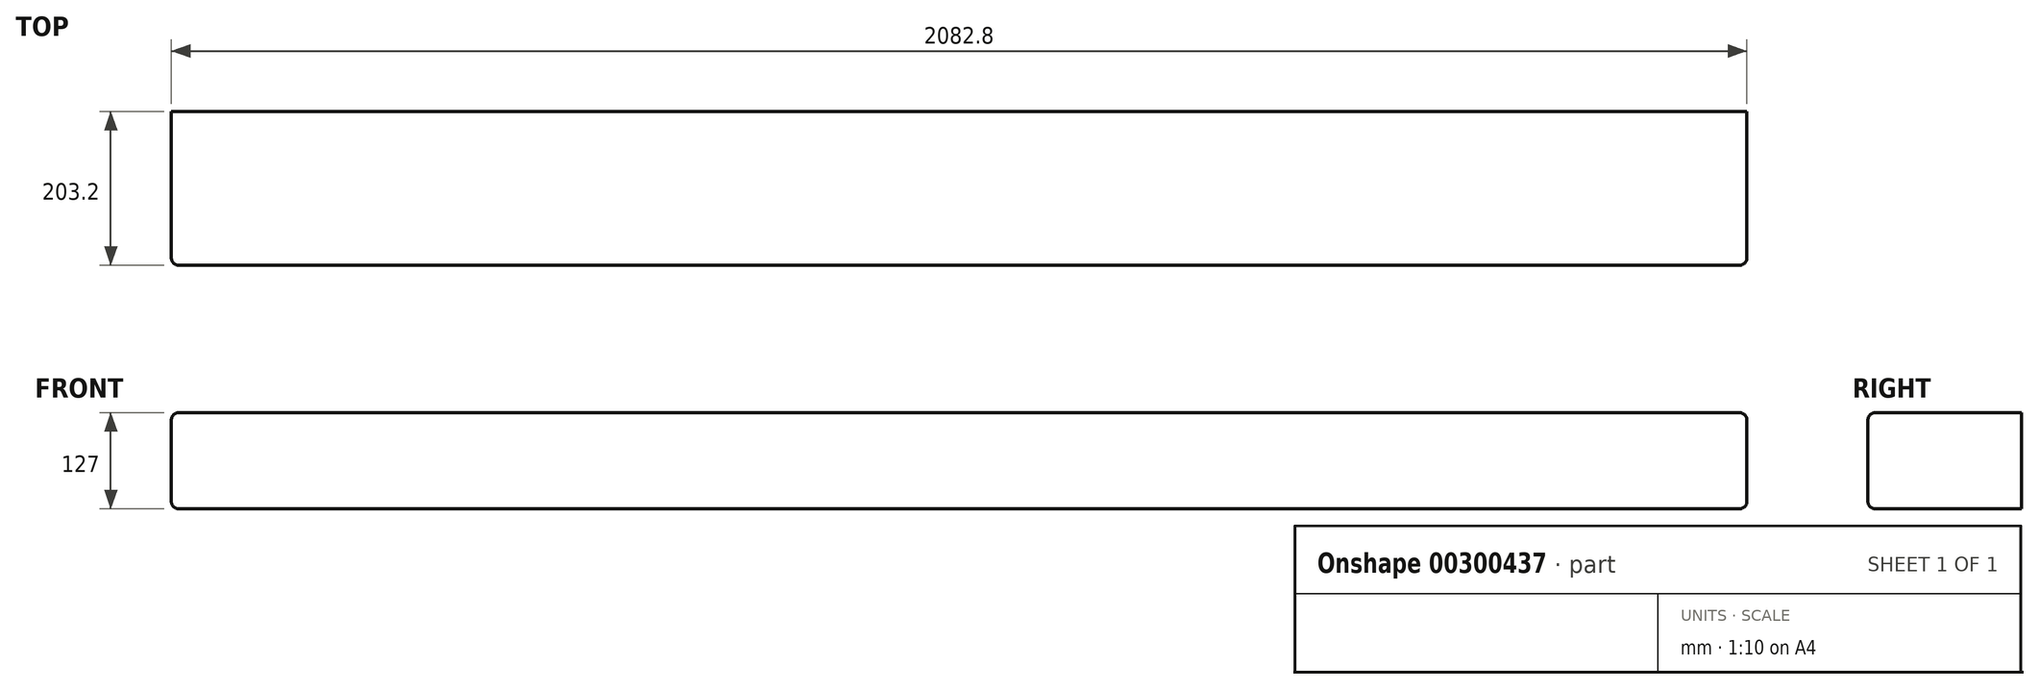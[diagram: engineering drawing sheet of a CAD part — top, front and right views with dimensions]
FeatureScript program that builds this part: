
annotation { "Feature Type Name" : "Feature", "Feature Type Description" : "" }
export const myFeature = defineFeature(function(context is Context, id is Id, definition is map)
    precondition{}
    {
        {
            var Q0;
            Q0=qCreatedBy(makeId("Right.planeOp"),FACE);
            var sketch = newSketch(context, id + "F0", { "sketchPlane" : qUnion([Q0])});
            skLineSegment(sketch, "E0.bottom", {"start": v(-101.6, 63.5) * mm, "end": v(101.6, 63.5) * mm});
            skLineSegment(sketch, "E0.top", {"start": v(-101.6, -63.5) * mm, "end": v(101.6, -63.5) * mm});
            skLineSegment(sketch, "E0.left", {"start": v(-101.6, 63.5) * mm, "end": v(-101.6, -63.5) * mm});
            skLineSegment(sketch, "E0.right", {"start": v(101.6, 63.5) * mm, "end": v(101.6, -63.5) * mm});
            skSolve(sketch);
        }
        {
            var Q0;
            Q0=makeQuery(id+"F0.imprint","IMPRINT",FACE,{"disambiguationData":[TD([[makeQuery(id+"F0.imprint","IMPRINT",EDGE,{"derivedFrom":sQuery(id+"F0.wireOp",EDGE,"E0.bottom")}),-1.0]])]});
            extrude(context, id + "F1", {"entities" : qUnion([Q0]), "endBound" : BoundingType.SYMMETRIC, "depth" : 2082.8 * mm});
        }
        {
            var Q0;
            Q0=makeQuery(id+"F1.opExtrude","SWEPT_EDGE",EDGE,{"disambiguationData":[OSD([sQuery(id+"F0.wireOp",EDGE,"E0.bottom"),sQuery(id+"F0.wireOp",EDGE,"E0.left")])]});
            var Q1;
            Q1=makeQuery(id+"F1.opExtrude","CAP_EDGE",EDGE,{"disambiguationData":[OSD([sQuery(id+"F0.wireOp",EDGE,"E0.bottom")])],"isStart":true});
            var Q2;
            Q2=makeQuery(id+"F1.opExtrude","CAP_EDGE",EDGE,{"disambiguationData":[OSD([sQuery(id+"F0.wireOp",EDGE,"E0.left")])],"isStart":true});
            var Q3;
            Q3=makeQuery(id+"F1.opExtrude","CAP_EDGE",EDGE,{"disambiguationData":[OSD([sQuery(id+"F0.wireOp",EDGE,"E0.top")])],"isStart":true});
            var Q4;
            Q4=makeQuery(id+"F1.opExtrude","SWEPT_EDGE",EDGE,{"disambiguationData":[OSD([sQuery(id+"F0.wireOp",EDGE,"E0.top"),sQuery(id+"F0.wireOp",EDGE,"E0.left")])]});
            var Q5;
            Q5=makeQuery(id+"F1.opExtrude","CAP_EDGE",EDGE,{"disambiguationData":[OSD([sQuery(id+"F0.wireOp",EDGE,"E0.bottom")])],"isStart":false});
            var Q6;
            Q6=makeQuery(id+"F1.opExtrude","CAP_EDGE",EDGE,{"disambiguationData":[OSD([sQuery(id+"F0.wireOp",EDGE,"E0.left")])],"isStart":false});
            var Q7;
            Q7=makeQuery(id+"F1.opExtrude","CAP_EDGE",EDGE,{"disambiguationData":[OSD([sQuery(id+"F0.wireOp",EDGE,"E0.top")])],"isStart":false});
            fillet(context, id + "F2", {"entities" : qUnion([Q0, Q1, Q2, Q3, Q4, Q5, Q6, Q7]), "radius" : 9.52 * mm, "tangentPropagation" : true, "allowEdgeOverflow" : false});
        }
    });
